# Revit family: Sanitary_Showers_hansgrohe_Pulsify-S-Showerpipe-260-1jet-with-Showe_NEW
name_source: partatom
category: Plumbing Fixtures
units: mm (PartAtom-declared; Revit-internal decimal feet)

## family parameters
Always vertical = No
Cut with Voids When Loaded = No
OmniClass Number = 23.31.17.00
OmniClass Title = Showers
Part Type = Normal
Room Calculation Point = No
Round Connector Dimension = Use Diameter
Shared = No
Work Plane-Based = Yes

## types (4) — shared parameters
Always visible = Yes
Connector Description = Water Inlet 12.7mm
Date Updated = 2023/12/06
Default Elevation = 1219 mm
Description = Pulsify S Showerpipe 260 1jet with ShowerTablet Select 400
Diameter = 13 mm
Manufacturer = Hansgrohe
Material 1 = Hansgrohe -  Plastic - Graphite
Model = 24220XXX
Product Guid = 751cca7a-4b14-40bd-b756-60a9f7db387f
Product Page URL = https://www.hansgrohe.com
Product data url = https://bimobject.com
URL = https://www.hansgrohe.com
Version = 2
zero-valued in all types: Edition number

## per-type parameters (varying)
| type | Material |
| 000 Chrome | Hansgrohe - Metal - 000 Chrome |
| 140 Brushed Bronze | Hansgrohe - Metal - 140 Brushed Bronze |
| 670 Matte Black | Hansgrohe - Metal - 670 Matte Black |
| 700 Matte White | Hansgrohe - Metal - 700 Matte White |

## geometry (parser evidence)
native form markers: Sweep x2
no freeform markers — native parametric forms only
